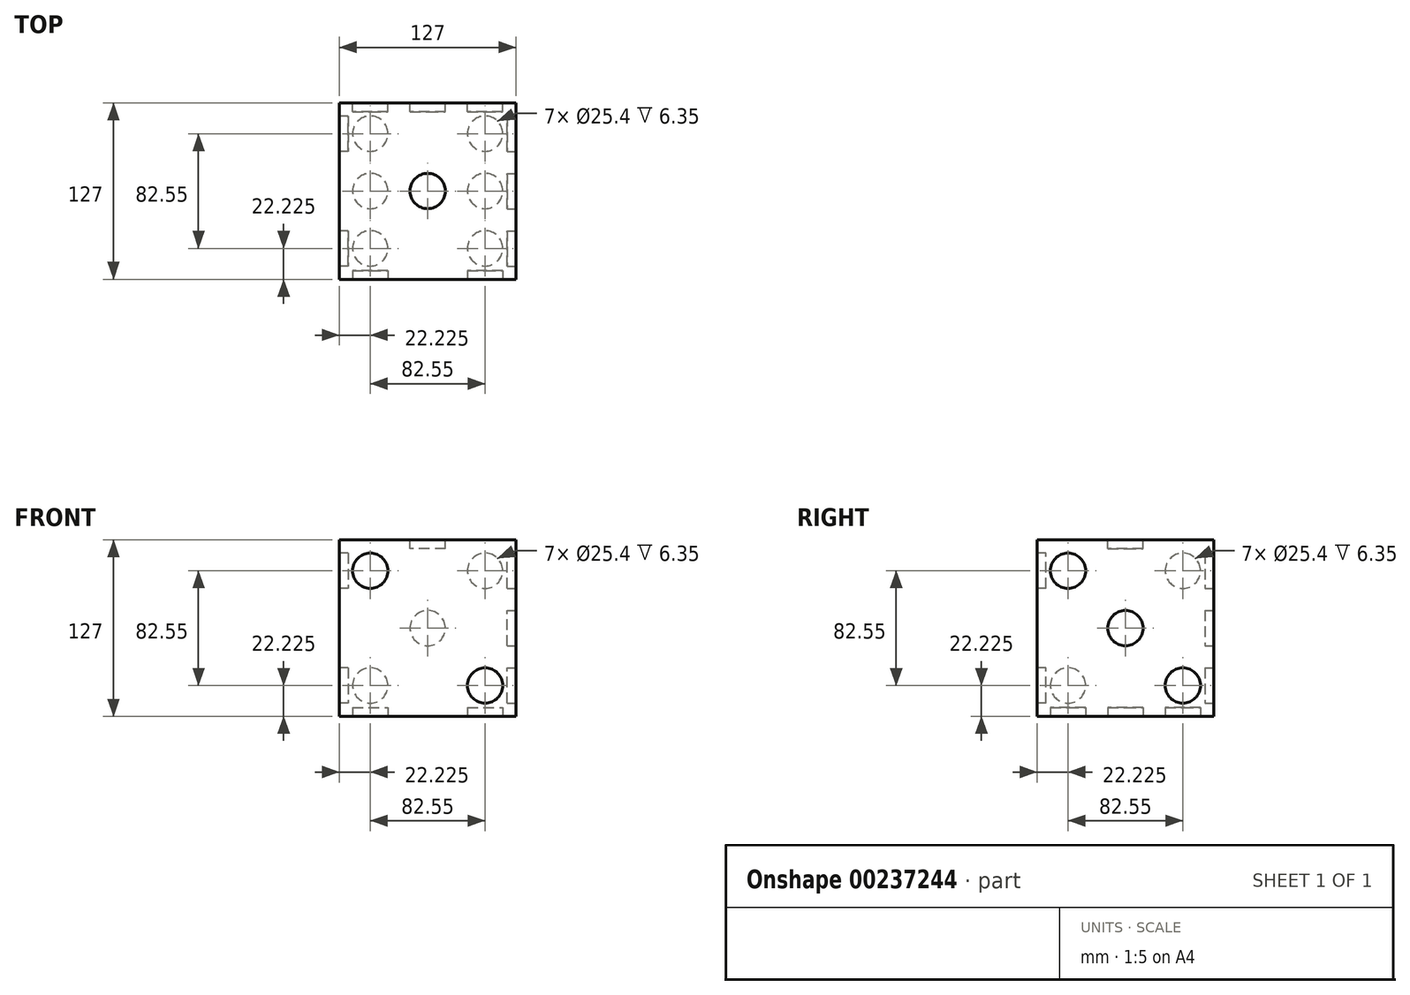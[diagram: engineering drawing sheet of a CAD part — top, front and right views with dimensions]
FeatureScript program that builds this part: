
annotation { "Feature Type Name" : "Feature", "Feature Type Description" : "" }
export const myFeature = defineFeature(function(context is Context, id is Id, definition is map)
    precondition{}
    {
        {
            var Q0;
            Q0=qCreatedBy(makeId("Top.planeOp"),FACE);
            var sketch = newSketch(context, id + "F0", { "sketchPlane" : qUnion([Q0])});
            skLineSegment(sketch, "E0.bottom", {"start": v(0, 0) * mm, "end": v(127, 0) * mm});
            skLineSegment(sketch, "E0.top", {"start": v(0, 127) * mm, "end": v(127, 127) * mm});
            skLineSegment(sketch, "E0.left", {"start": v(0, 0) * mm, "end": v(0, 127) * mm});
            skLineSegment(sketch, "E0.right", {"start": v(127, 0) * mm, "end": v(127, 127) * mm});
            skSolve(sketch);
        }
        {
            var Q0;
            Q0=makeQuery(id+"F0.imprint","IMPRINT",FACE,{"disambiguationData":[TD([[makeQuery(id+"F0.imprint","IMPRINT",EDGE,{"derivedFrom":sQuery(id+"F0.wireOp",EDGE,"E0.bottom")}),1.0]])]});
            extrude(context, id + "F1", {"entities" : qUnion([Q0]), "depth" : 127 * mm});
        }
        {
            var Q0;
            Q0=makeQuery(id+"F1.opExtrude","CAP_FACE",FACE,{"disambiguationData":[OSD([sQuery(id+"F0.wireOp",EDGE,"E0.bottom"),sQuery(id+"F0.wireOp",EDGE,"E0.top"),sQuery(id+"F0.wireOp",EDGE,"E0.left"),sQuery(id+"F0.wireOp",EDGE,"E0.right")])],"isStart":false});
            var sketch = newSketch(context, id + "F2", { "sketchPlane" : qUnion([Q0])});
            skCircle(sketch, "E1", {"center": v(63.5, 63.5) * mm, "radius": 12.7 * mm});
            skPoint(sketch, "E2", {"position": v(127, 63.5) * mm});
            skPoint(sketch, "E3", {"position": v(63.5, 0) * mm});
            skSolve(sketch);
        }
        {
            var Q0;
            Q0=makeQuery(id+"F2.imprint","IMPRINT",FACE,{"disambiguationData":[TD([[makeQuery(id+"F2.imprint","IMPRINT",EDGE,{"derivedFrom":sQuery(id+"F2.wireOp",EDGE,"E1")}),1.0]])]});
            extrude(context, id + "F3", {"entities" : qUnion([Q0]), "operationType" : NewBodyOperationType.REMOVE, "oppositeDirection" : true, "depth" : 6.35 * mm});
        }
        {
            var Q0;
            Q0=makeQuery(id+"F1.opExtrude","SWEPT_FACE",FACE,{"disambiguationData":[OSD([sQuery(id+"F0.wireOp",EDGE,"E0.bottom")])]});
            var sketch = newSketch(context, id + "F4", { "sketchPlane" : qUnion([Q0])});
            skCircle(sketch, "E4", {"center": v(104.78, 22.22) * mm, "radius": 12.7 * mm});
            skSolve(sketch);
        }
        {
            var Q0;
            Q0=makeQuery(id+"F4.imprint","IMPRINT",FACE,{"disambiguationData":[TD([[makeQuery(id+"F4.imprint","IMPRINT",EDGE,{"derivedFrom":sQuery(id+"F4.wireOp",EDGE,"E4")}),1.0]])]});
            extrude(context, id + "F5", {"entities" : qUnion([Q0]), "operationType" : NewBodyOperationType.REMOVE, "oppositeDirection" : true, "depth" : 6.35 * mm});
        }
        {
            var Q0;
            Q0=makeQuery(id+"F1.opExtrude","SWEPT_FACE",FACE,{"disambiguationData":[OSD([sQuery(id+"F0.wireOp",EDGE,"E0.bottom")])]});
            var sketch = newSketch(context, id + "F6", { "sketchPlane" : qUnion([Q0])});
            skCircle(sketch, "E5", {"center": v(22.23, 104.78) * mm, "radius": 12.7 * mm});
            skSolve(sketch);
        }
        {
            var Q0;
            Q0=makeQuery(id+"F6.imprint","IMPRINT",FACE,{"disambiguationData":[TD([[makeQuery(id+"F6.imprint","IMPRINT",EDGE,{"derivedFrom":sQuery(id+"F6.wireOp",EDGE,"E5")}),1.0]])]});
            extrude(context, id + "F7", {"entities" : qUnion([Q0]), "operationType" : NewBodyOperationType.REMOVE, "oppositeDirection" : true, "depth" : 6.35 * mm});
        }
        {
            var Q0;
            Q0=makeQuery(id+"F1.opExtrude","SWEPT_FACE",FACE,{"disambiguationData":[OSD([sQuery(id+"F0.wireOp",EDGE,"E0.right")])]});
            var sketch = newSketch(context, id + "F8", { "sketchPlane" : qUnion([Q0])});
            skCircle(sketch, "E6", {"center": v(22.22, 104.78) * mm, "radius": 12.7 * mm});
            skCircle(sketch, "E7", {"center": v(104.77, 22.22) * mm, "radius": 12.7 * mm});
            skCircle(sketch, "E8", {"center": v(63.5, 63.5) * mm, "radius": 12.7 * mm});
            skSolve(sketch);
        }
        {
            var Q0;
            Q0=makeQuery(id+"F8.imprint","IMPRINT",FACE,{"disambiguationData":[TD([[makeQuery(id+"F8.imprint","IMPRINT",EDGE,{"derivedFrom":sQuery(id+"F8.wireOp",EDGE,"E6")}),1.0]])]});
            var Q1;
            Q1=makeQuery(id+"F8.imprint","IMPRINT",FACE,{"disambiguationData":[TD([[makeQuery(id+"F8.imprint","IMPRINT",EDGE,{"derivedFrom":sQuery(id+"F8.wireOp",EDGE,"E7")}),1.0]])]});
            extrude(context, id + "F9", {"entities" : qUnion([Q0, Q1]), "operationType" : NewBodyOperationType.REMOVE, "oppositeDirection" : true, "depth" : 6.35 * mm});
        }
        {
            var Q0;
            Q0 = qSketchRegion(id + "F8", true);
            extrude(context, id + "F10", {"entities" : qUnion([Q0]), "operationType" : NewBodyOperationType.REMOVE, "oppositeDirection" : true, "depth" : 6.35 * mm});
        }
        {
            var Q0;
            Q0=makeQuery(id+"F1.opExtrude","SWEPT_FACE",FACE,{"disambiguationData":[OSD([sQuery(id+"F0.wireOp",EDGE,"E0.left")])]});
            var sketch = newSketch(context, id + "F11", { "sketchPlane" : qUnion([Q0])});
            skCircle(sketch, "E9", {"center": v(-22.23, 22.22) * mm, "radius": 12.7 * mm});
            skCircle(sketch, "E10", {"center": v(-22.23, 104.78) * mm, "radius": 12.7 * mm});
            skCircle(sketch, "E11", {"center": v(-104.78, 22.22) * mm, "radius": 12.7 * mm});
            skCircle(sketch, "E12", {"center": v(-104.78, 104.78) * mm, "radius": 12.7 * mm});
            skSolve(sketch);
        }
        {
            var Q0;
            Q0=makeQuery(id+"F11.imprint","IMPRINT",FACE,{"disambiguationData":[TD([[makeQuery(id+"F11.imprint","IMPRINT",EDGE,{"derivedFrom":sQuery(id+"F11.wireOp",EDGE,"E10")}),1.0]])]});
            var Q1;
            Q1=makeQuery(id+"F11.imprint","IMPRINT",FACE,{"disambiguationData":[TD([[makeQuery(id+"F11.imprint","IMPRINT",EDGE,{"derivedFrom":sQuery(id+"F11.wireOp",EDGE,"E12")}),1.0]])]});
            var Q2;
            Q2=makeQuery(id+"F11.imprint","IMPRINT",FACE,{"disambiguationData":[TD([[makeQuery(id+"F11.imprint","IMPRINT",EDGE,{"derivedFrom":sQuery(id+"F11.wireOp",EDGE,"E11")}),1.0]])]});
            var Q3;
            Q3=makeQuery(id+"F11.imprint","IMPRINT",FACE,{"disambiguationData":[TD([[makeQuery(id+"F11.imprint","IMPRINT",EDGE,{"derivedFrom":sQuery(id+"F11.wireOp",EDGE,"E9")}),1.0]])]});
            extrude(context, id + "F12", {"entities" : qUnion([Q0, Q1, Q2, Q3]), "operationType" : NewBodyOperationType.REMOVE, "oppositeDirection" : true, "depth" : 6.35 * mm});
        }
        {
            var Q0;
            Q0=makeQuery(id+"F1.opExtrude","SWEPT_FACE",FACE,{"disambiguationData":[OSD([sQuery(id+"F0.wireOp",EDGE,"E0.top")])]});
            var sketch = newSketch(context, id + "F13", { "sketchPlane" : qUnion([Q0])});
            skCircle(sketch, "E13", {"center": v(-104.77, 104.78) * mm, "radius": 12.7 * mm});
            skCircle(sketch, "E14", {"center": v(-104.77, 22.22) * mm, "radius": 12.7 * mm});
            skCircle(sketch, "E15", {"center": v(-22.23, 104.78) * mm, "radius": 12.7 * mm});
            skCircle(sketch, "E16", {"center": v(-22.23, 22.22) * mm, "radius": 12.7 * mm});
            skCircle(sketch, "E17", {"center": v(-63.5, 63.5) * mm, "radius": 12.7 * mm});
            skSolve(sketch);
        }
        {
            var Q0;
            Q0 = qSketchRegion(id + "F13", true);
            extrude(context, id + "F14", {"entities" : qUnion([Q0]), "operationType" : NewBodyOperationType.REMOVE, "oppositeDirection" : true, "depth" : 6.35 * mm});
        }
        {
            var Q0;
            Q0=makeQuery(id+"F1.opExtrude","CAP_FACE",FACE,{"disambiguationData":[OSD([sQuery(id+"F0.wireOp",EDGE,"E0.bottom"),sQuery(id+"F0.wireOp",EDGE,"E0.top"),sQuery(id+"F0.wireOp",EDGE,"E0.left"),sQuery(id+"F0.wireOp",EDGE,"E0.right")])],"isStart":true});
            var sketch = newSketch(context, id + "F15", { "sketchPlane" : qUnion([Q0])});
            skCircle(sketch, "E18", {"center": v(22.23, -22.23) * mm, "radius": 12.7 * mm});
            skCircle(sketch, "E19", {"center": v(22.23, -63.5) * mm, "radius": 12.7 * mm});
            skCircle(sketch, "E20", {"center": v(22.23, -104.78) * mm, "radius": 12.7 * mm});
            skCircle(sketch, "E21", {"center": v(104.78, -22.23) * mm, "radius": 12.7 * mm});
            skCircle(sketch, "E22", {"center": v(104.78, -63.5) * mm, "radius": 12.7 * mm});
            skCircle(sketch, "E23", {"center": v(104.77, -104.78) * mm, "radius": 12.7 * mm});
            skSolve(sketch);
        }
        {
            var Q0;
            Q0 = qSketchRegion(id + "F15", true);
            extrude(context, id + "F16", {"entities" : qUnion([Q0]), "operationType" : NewBodyOperationType.REMOVE, "oppositeDirection" : true, "depth" : 6.35 * mm});
        }
    });
